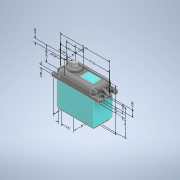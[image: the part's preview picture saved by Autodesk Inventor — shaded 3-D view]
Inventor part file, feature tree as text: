
AUTODESK INVENTOR PART (.ipt)
format: ipt  version: 2022 (Build 260153000, 153)  size: 264,192 bytes
history: mixed  units: mm
features: other x19, fillet x1, imported_body x1
ambient origin geometry x8: Origin, YZ Plane, XZ Plane, XY Plane, X Axis, Y Axis, Z Axis, Center Point
bodies: Solid1 (imported_parasolid)
feature tree (21):
  other  "Annotations"
  fillet  "Fillet8"  [1 undecoded]
  other  "Linear Dimension 3"
  other  "Linear Dimension 4"
  other  "Linear Dimension 5"
  other  "Linear Dimension 6"
  other  "Linear Dimension 7"
  other  "Linear Dimension 8"
  other  "Linear Dimension 9"
  other  "Linear Dimension 10"
  other  "Linear Dimension 11"
  other  "Radial Dimension 1"
  other  "Diameter Dimension 1"
  other  "Linear Dimension 12"
  other  "Linear Dimension 13"
  other  "Linear Dimension 14"
  other  "Linear Dimension 15"
  other  "Linear Dimension 16"
  other  "Linear Dimension 17"
  other  "Linear Dimension 18"
  imported_body  NMx_Import_Brep_tag  [imported B-rep: ~93 faces, bbox_mm=[53.85, 46.0, 20.7]]
note: 1 required parameter value undecoded (feature->parameter linkage not recoverable at this tier; creation-order binding heuristic only, values carry confidence <= 0.55)
